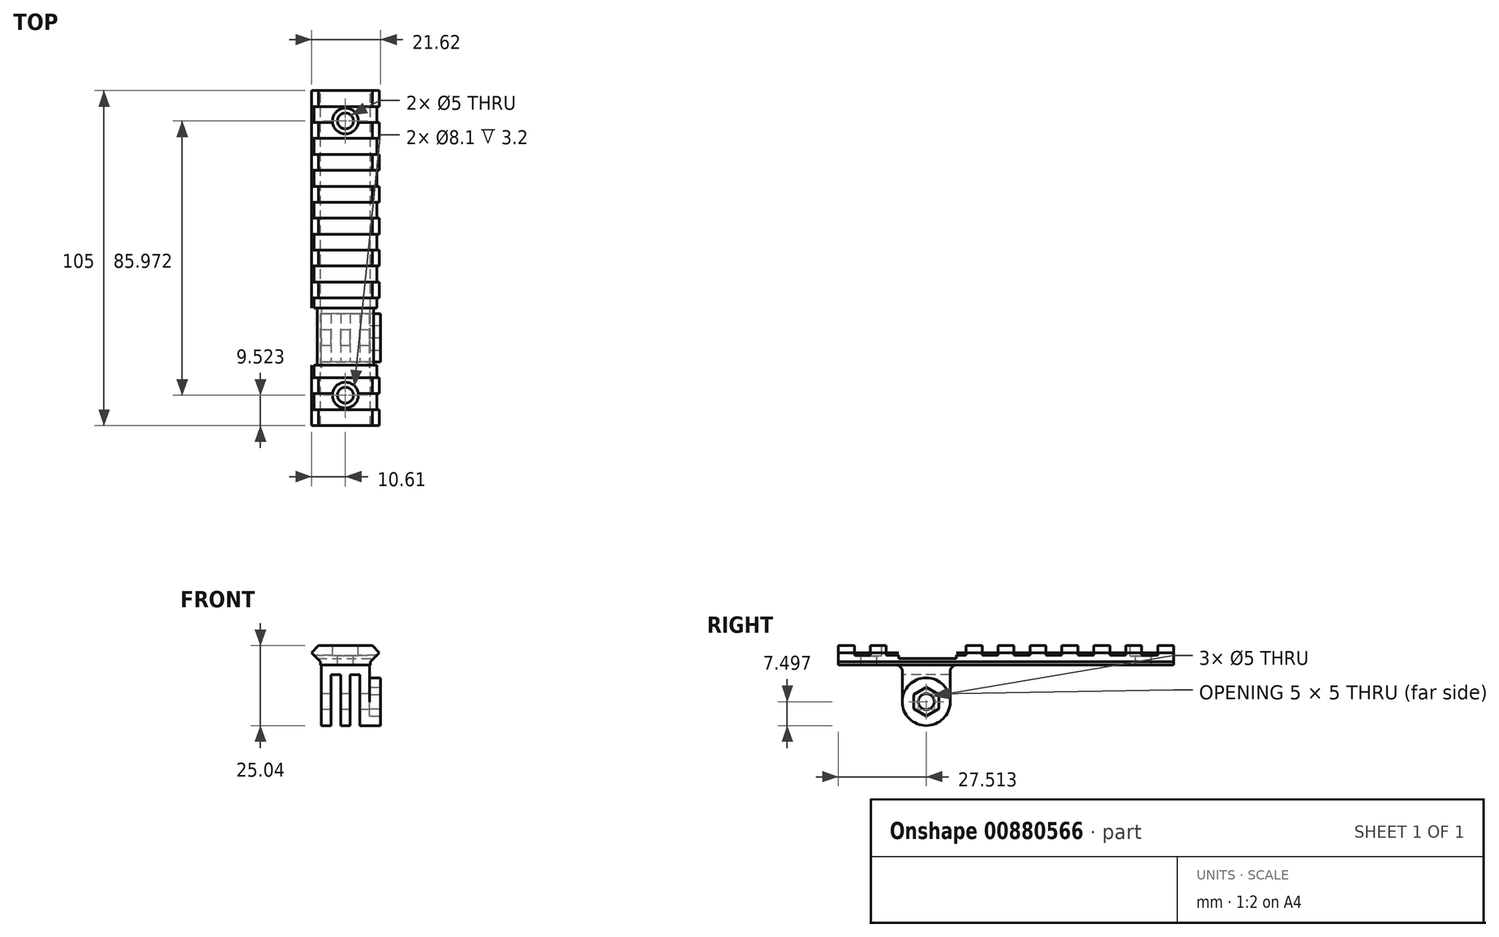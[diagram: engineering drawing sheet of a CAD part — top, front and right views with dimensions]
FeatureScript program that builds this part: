
annotation { "Feature Type Name" : "Feature", "Feature Type Description" : "" }
export const myFeature = defineFeature(function(context is Context, id is Id, definition is map)
    precondition{}
    {
        {
            var Q0;
            Q0=qCreatedBy(makeId("Front.planeOp"),FACE);
            var sketch = newSketch(context, id + "F0", { "sketchPlane" : qUnion([Q0])});
            skLineSegment(sketch, "E0", {"start": v(-7.8, -3.01) * mm, "end": v(7.81, -3.01) * mm});
            skLineSegment(sketch, "E1", {"start": v(7.81, -3.01) * mm, "end": v(7.81, -1.98) * mm});
            skLineSegment(sketch, "E2", {"start": v(7.81, -1.98) * mm, "end": v(10.6, 0.79) * mm});
            skLineSegment(sketch, "E3", {"start": v(10.6, 0.79) * mm, "end": v(8.39, 3.03) * mm});
            skLineSegment(sketch, "E4", {"start": v(8.39, 3.03) * mm, "end": v(-8.4, 3.03) * mm});
            skLineSegment(sketch, "E5", {"start": v(-8.4, 3.03) * mm, "end": v(-10.6, 0.79) * mm});
            skLineSegment(sketch, "E6", {"start": v(-10.6, 0.79) * mm, "end": v(-7.8, -1.98) * mm});
            skLineSegment(sketch, "E7", {"start": v(-7.8, -1.98) * mm, "end": v(-7.8, -3.01) * mm});
            skSolve(sketch);
        }
        {
            var Q0;
            Q0=qSketchRegion(id+"F0",true);
            extrude(context, id + "F1", {"entities" : qUnion([Q0]), "endBound" : BoundingType.SYMMETRIC, "depth" : 105 * mm, "offsetDistance" : 25 * mm});
        }
        {
            var Q0;
            Q0=qCreatedBy(makeId("Top.planeOp"),FACE);
            var sketch = newSketch(context, id + "F2", { "sketchPlane" : qUnion([Q0])});
            skLineSegment(sketch, "E8.bottom", {"start": v(10.61, -7.5) * mm, "end": v(-10.6, -7.5) * mm});
            skLineSegment(sketch, "E8.top", {"start": v(10.61, -2.5) * mm, "end": v(-10.6, -2.5) * mm});
            skLineSegment(sketch, "E8.left", {"start": v(10.61, -7.5) * mm, "end": v(10.61, -2.5) * mm});
            skLineSegment(sketch, "E8.right", {"start": v(-10.6, -7.5) * mm, "end": v(-10.6, -2.5) * mm});
            skLineSegment(sketch, "E9.0.1.0", {"start": v(10.61, -17.5) * mm, "end": v(-10.6, -17.5) * mm});
            skLineSegment(sketch, "E9.0.1.1", {"start": v(10.61, -12.5) * mm, "end": v(-10.6, -12.5) * mm});
            skLineSegment(sketch, "E9.0.1.2", {"start": v(10.61, -17.5) * mm, "end": v(10.61, -12.5) * mm});
            skLineSegment(sketch, "E9.0.1.3", {"start": v(-10.6, -17.5) * mm, "end": v(-10.6, -12.5) * mm});
            skLineSegment(sketch, "E9.0.2.0", {"start": v(10.61, -27.5) * mm, "end": v(-10.6, -27.5) * mm});
            skLineSegment(sketch, "E9.0.2.1", {"start": v(10.61, -22.5) * mm, "end": v(-10.6, -22.5) * mm});
            skLineSegment(sketch, "E9.0.2.2", {"start": v(10.61, -27.5) * mm, "end": v(10.61, -22.5) * mm});
            skLineSegment(sketch, "E9.0.2.3", {"start": v(-10.6, -27.5) * mm, "end": v(-10.6, -22.5) * mm});
            skLineSegment(sketch, "E9.0.3.0", {"start": v(10.61, -37.5) * mm, "end": v(-10.6, -37.5) * mm});
            skLineSegment(sketch, "E9.0.3.1", {"start": v(10.61, -32.5) * mm, "end": v(-10.6, -32.5) * mm});
            skLineSegment(sketch, "E9.0.3.2", {"start": v(10.61, -37.5) * mm, "end": v(10.61, -32.5) * mm});
            skLineSegment(sketch, "E9.0.3.3", {"start": v(-10.6, -37.5) * mm, "end": v(-10.6, -32.5) * mm});
            skLineSegment(sketch, "E9.0.4.0", {"start": v(10.61, -47.5) * mm, "end": v(-10.6, -47.5) * mm});
            skLineSegment(sketch, "E9.0.4.1", {"start": v(10.61, -42.5) * mm, "end": v(-10.6, -42.5) * mm});
            skLineSegment(sketch, "E9.0.4.2", {"start": v(10.61, -47.5) * mm, "end": v(10.61, -42.5) * mm});
            skLineSegment(sketch, "E9.0.4.3", {"start": v(-10.6, -47.5) * mm, "end": v(-10.6, -42.5) * mm});
            skLineSegment(sketch, "E9.direction1", {"start": v(-10.6, -7.5) * mm, "end": v(14.4, -7.5) * mm, "construction": true});
            skLineSegment(sketch, "E9.direction2", {"start": v(-10.6, -7.5) * mm, "end": v(-10.6, -17.5) * mm, "construction": true});
            skLineSegment(sketch, "E10.0.1.0", {"start": v(10.61, 7.5) * mm, "end": v(-10.6, 7.5) * mm});
            skLineSegment(sketch, "E10.0.1.1", {"start": v(10.61, 2.5) * mm, "end": v(10.61, 7.5) * mm});
            skLineSegment(sketch, "E10.0.1.2", {"start": v(-10.6, 2.5) * mm, "end": v(-10.6, 7.5) * mm});
            skLineSegment(sketch, "E10.0.1.3", {"start": v(10.61, 2.5) * mm, "end": v(-10.6, 2.5) * mm});
            skLineSegment(sketch, "E10.0.2.0", {"start": v(10.61, 17.5) * mm, "end": v(-10.6, 17.5) * mm});
            skLineSegment(sketch, "E10.0.2.1", {"start": v(10.61, 12.5) * mm, "end": v(10.61, 17.5) * mm});
            skLineSegment(sketch, "E10.0.2.2", {"start": v(-10.6, 12.5) * mm, "end": v(-10.6, 17.5) * mm});
            skLineSegment(sketch, "E10.0.2.3", {"start": v(10.61, 12.5) * mm, "end": v(-10.6, 12.5) * mm});
            skLineSegment(sketch, "E10.0.3.0", {"start": v(10.61, 27.5) * mm, "end": v(-10.6, 27.5) * mm});
            skLineSegment(sketch, "E10.0.3.1", {"start": v(10.61, 22.5) * mm, "end": v(10.61, 27.5) * mm});
            skLineSegment(sketch, "E10.0.3.2", {"start": v(-10.6, 22.5) * mm, "end": v(-10.6, 27.5) * mm});
            skLineSegment(sketch, "E10.0.3.3", {"start": v(10.61, 22.5) * mm, "end": v(-10.6, 22.5) * mm});
            skLineSegment(sketch, "E10.0.4.0", {"start": v(10.61, 37.5) * mm, "end": v(-10.6, 37.5) * mm});
            skLineSegment(sketch, "E10.0.4.1", {"start": v(10.61, 32.5) * mm, "end": v(10.61, 37.5) * mm});
            skLineSegment(sketch, "E10.0.4.2", {"start": v(-10.6, 32.5) * mm, "end": v(-10.6, 37.5) * mm});
            skLineSegment(sketch, "E10.0.4.3", {"start": v(10.61, 32.5) * mm, "end": v(-10.6, 32.5) * mm});
            skLineSegment(sketch, "E10.0.5.0", {"start": v(10.61, 47.5) * mm, "end": v(-10.6, 47.5) * mm});
            skLineSegment(sketch, "E10.0.5.1", {"start": v(10.61, 42.5) * mm, "end": v(10.61, 47.5) * mm});
            skLineSegment(sketch, "E10.0.5.2", {"start": v(-10.6, 42.5) * mm, "end": v(-10.6, 47.5) * mm});
            skLineSegment(sketch, "E10.0.5.3", {"start": v(10.61, 42.5) * mm, "end": v(-10.6, 42.5) * mm});
            skLineSegment(sketch, "E10.direction1", {"start": v(-10.6, -2.5) * mm, "end": v(14.4, -2.5) * mm, "construction": true});
            skLineSegment(sketch, "E10.direction2", {"start": v(-10.6, -2.5) * mm, "end": v(-10.6, 7.5) * mm, "construction": true});
            skSolve(sketch);
        }
        {
            var Q0;
            Q0=qSketchRegion(id+"F2",true);
            extrude(context, id + "F3", {"entities" : qUnion([Q0]), "operationType" : NewBodyOperationType.REMOVE, "depth" : 5 * mm, "offsetDistance" : 25 * mm});
        }
        {
            var Q0;
            Q0=makeQuery(id+"F3.boolean.opBoolean","SPLIT",FACE,{"disambiguationData":[TD([makeQuery(id+"F3.opExtrude","SWEPT_FACE",FACE,{"disambiguationData":[OSD([sQuery(id+"F2.wireOp",EDGE,"E10.0.4.0")])]})])],"derivedFrom":makeQuery(id+"F1.opExtrude","SWEPT_FACE",FACE,{"disambiguationData":[OSD([sQuery(id+"F0.wireOp",EDGE,"E4")])]})});
            var sketch = newSketch(context, id + "F4", { "sketchPlane" : qUnion([Q0])});
            skPoint(sketch, "E11", {"position": v(0, 43) * mm});
            skPoint(sketch, "E12", {"position": v(0, -42.98) * mm});
            skSolve(sketch);
        }
        {
            var Q0;
            Q0=sQuery(id+"F4.wireOp",VERTEX,"E11");
            var Q1;
            Q1=makeQuery(id+"F1.opExtrude","SWEPT_BODY",BODY,{"disambiguationData":[OSD([sQuery(id+"F0.wireOp",EDGE,"E0"),sQuery(id+"F0.wireOp",EDGE,"E1"),sQuery(id+"F0.wireOp",EDGE,"E2"),sQuery(id+"F0.wireOp",EDGE,"E3"),sQuery(id+"F0.wireOp",EDGE,"E4"),sQuery(id+"F0.wireOp",EDGE,"E5"),sQuery(id+"F0.wireOp",EDGE,"E6"),sQuery(id+"F0.wireOp",EDGE,"E7")])]});
            hole(context, id + "F5", {"style" : HoleStyle.C_BORE, "endStyle" : HoleEndStyle.BLIND, "holeDiameter" : 5 * mm, "cBoreDiameter" : 8.1 * mm, "cBoreDepth" : 3.2 * mm, "majorDiameter" : 5 * mm, "holeDepth" : 6.1 * mm, "isTappedThrough" : true, "tappedDepth" : 12 * mm, "tapClearance" : 3, "startFromSketch" : true, "locations" : qUnion([Q0]), "scope" : qUnion([Q1])});
        }
        {
            var Q0;
            Q0=sQuery(id+"F4.wireOp",VERTEX,"E12");
            var Q1;
            Q1=makeQuery(id+"F1.opExtrude","SWEPT_BODY",BODY,{"disambiguationData":[OSD([sQuery(id+"F0.wireOp",EDGE,"E0"),sQuery(id+"F0.wireOp",EDGE,"E1"),sQuery(id+"F0.wireOp",EDGE,"E2"),sQuery(id+"F0.wireOp",EDGE,"E3"),sQuery(id+"F0.wireOp",EDGE,"E4"),sQuery(id+"F0.wireOp",EDGE,"E5"),sQuery(id+"F0.wireOp",EDGE,"E6"),sQuery(id+"F0.wireOp",EDGE,"E7")])]});
            hole(context, id + "F6", {"style" : HoleStyle.C_BORE, "endStyle" : HoleEndStyle.BLIND, "holeDiameter" : 5 * mm, "cBoreDiameter" : 8.1 * mm, "cBoreDepth" : 3.2 * mm, "majorDiameter" : 5 * mm, "holeDepth" : 6.1 * mm, "isTappedThrough" : true, "tappedDepth" : 12 * mm, "tapClearance" : 3, "startFromSketch" : true, "locations" : qUnion([Q0]), "scope" : qUnion([Q1])});
        }
        {
            var Q0;
            Q0=makeQuery(id+"F1.opExtrude","SWEPT_FACE",FACE,{"disambiguationData":[OSD([sQuery(id+"F0.wireOp",EDGE,"E0")])]});
            var sketch = newSketch(context, id + "F7", { "sketchPlane" : qUnion([Q0])});
            skLineSegment(sketch, "E13.bottom", {"start": v(-114.09, 45.69) * mm, "end": v(-86.59, 45.69) * mm});
            skLineSegment(sketch, "E13.top", {"start": v(-114.09, 30.69) * mm, "end": v(-86.59, 30.69) * mm});
            skLineSegment(sketch, "E13.left", {"start": v(-121.59, 38.19) * mm, "end": v(-121.59, 38.19) * mm});
            skLineSegment(sketch, "E13.right", {"start": v(-86.59, 45.69) * mm, "end": v(-86.59, 30.69) * mm});
            skLineSegment(sketch, "E14", {"start": v(-121.59, 30.69) * mm, "end": v(-86.59, 45.69) * mm, "construction": true});
            skLineSegment(sketch, "E15", {"start": v(-121.59, 45.69) * mm, "end": v(-86.59, 30.69) * mm, "construction": true});
            skPoint(sketch, "E16.visualSharp", {"position": v(-121.59, 45.69) * mm});
            skArc(sketch, "E16.filletArc", {"start": v(-114.09, 45.69) * mm, "mid": v(-119.4, 43.5) * mm, "end": v(-121.59, 38.19) * mm});
            skPoint(sketch, "E17.visualSharp", {"position": v(-121.59, 30.69) * mm});
            skArc(sketch, "E17.filletArc", {"start": v(-121.59, 38.19) * mm, "mid": v(-119.4, 32.88) * mm, "end": v(-114.09, 30.69) * mm});
            skCircle(sketch, "E18", {"center": v(-114.09, 38.19) * mm, "radius": 2.5 * mm});
            skCircle(sketch, "E19", {"center": v(-114.09, 38.19) * mm, "radius": 7.5 * mm});
            skSolve(sketch);
        }
        {
            var Q0;
            Q0 = qSketchRegion(id + "F7", true);
            extrude(context, id + "F8", {"entities" : qUnion([Q0]), "depth" : 15 * mm, "offsetDistance" : 25 * mm});
        }
        {
            var Q0;
            Q0=makeQuery(id+"F7.imprint","IMPRINT",FACE,{"disambiguationData":[TD([[makeQuery(id+"F7.imprint","IMPRINT",EDGE,{"derivedFrom":sQuery(id+"F7.wireOp",EDGE,"E18")}),-1.0]])]});
            extrude(context, id + "F9", {"entities" : qUnion([Q0]), "operationType" : NewBodyOperationType.ADD, "depth" : 18.5 * mm, "offsetDistance" : 25 * mm});
        }
        {
            var Q0;
            Q0=makeQuery(id+"F9.opExtrude","CAP_FACE",FACE,{"disambiguationData":[OSD([sQuery(id+"F7.wireOp",EDGE,"E18"),sQuery(id+"F7.wireOp",EDGE,"E19")])],"isStart":false});
            var sketch = newSketch(context, id + "F10", { "sketchPlane" : qUnion([Q0])});
            skLineSegment(sketch, "E20", {"start": v(-114.09, 38.19) * mm, "end": v(-109.59, 38.19) * mm, "construction": true});
            skCircle(sketch, "E21.cCircle", {"center": v(-114.09, 38.19) * mm, "radius": 4.5 * mm, "construction": true});
            skLineSegment(sketch, "E21.0", {"start": v(-109.59, 38.19) * mm, "end": v(-111.84, 34.3) * mm});
            skLineSegment(sketch, "E21.1", {"start": v(-111.84, 34.3) * mm, "end": v(-116.34, 34.3) * mm});
            skLineSegment(sketch, "E21.2", {"start": v(-116.34, 34.3) * mm, "end": v(-118.59, 38.19) * mm});
            skLineSegment(sketch, "E21.3", {"start": v(-118.59, 38.19) * mm, "end": v(-116.34, 42.08) * mm});
            skLineSegment(sketch, "E21.4", {"start": v(-116.34, 42.08) * mm, "end": v(-111.84, 42.08) * mm});
            skLineSegment(sketch, "E21.5", {"start": v(-111.84, 42.08) * mm, "end": v(-109.59, 38.19) * mm});
            skSolve(sketch);
        }
        {
            var Q0;
            Q0 = qSketchRegion(id + "F10", true);
            extrude(context, id + "F11", {"entities" : qUnion([Q0]), "operationType" : NewBodyOperationType.REMOVE, "oppositeDirection" : true, "depth" : 3.5 * mm, "offsetDistance" : 25 * mm});
        }
        {
            var Q0;
            Q0=makeQuery(id+"F8.opExtrude","CAP_FACE",FACE,{"disambiguationData":[OSD([sQuery(id+"F7.wireOp",EDGE,"E13.bottom"),sQuery(id+"F7.wireOp",EDGE,"E13.top"),sQuery(id+"F7.wireOp",EDGE,"E13.right"),sQuery(id+"F7.wireOp",EDGE,"E18"),sQuery(id+"F7.wireOp",EDGE,"E19")])],"isStart":true});
            var sketch = newSketch(context, id + "F12", { "sketchPlane" : qUnion([Q0])});
            skLineSegment(sketch, "E22.bottom", {"start": v(-105.66, -30.69) * mm, "end": v(-121.66, -30.69) * mm});
            skLineSegment(sketch, "E22.top", {"start": v(-105.66, -45.69) * mm, "end": v(-121.66, -45.69) * mm});
            skLineSegment(sketch, "E22.left", {"start": v(-105.66, -30.69) * mm, "end": v(-105.66, -45.69) * mm});
            skLineSegment(sketch, "E22.right", {"start": v(-121.66, -30.69) * mm, "end": v(-121.66, -45.69) * mm});
            skSolve(sketch);
        }
        {
            var Q0;
            Q0 = qSketchRegion(id + "F12", true);
            extrude(context, id + "F13", {"entities" : qUnion([Q0]), "operationType" : NewBodyOperationType.REMOVE, "oppositeDirection" : true, "depth" : 6 * mm, "offsetDistance" : 25 * mm, "hasSecondDirection" : true, "secondDirectionOppositeDirection" : true, "secondDirectionDepth" : 3 * mm});
        }
        {
            var Q0;
            Q0 = qSketchRegion(id + "F12", true);
            extrude(context, id + "F14", {"entities" : qUnion([Q0]), "operationType" : NewBodyOperationType.REMOVE, "oppositeDirection" : true, "depth" : 12 * mm, "offsetDistance" : 25 * mm, "hasSecondDirection" : true, "secondDirectionOppositeDirection" : true, "secondDirectionDepth" : 9 * mm});
        }
        {
            var Q0;
            Q0=makeQuery(id+"F8.opExtrude","SWEPT_BODY",BODY,{"disambiguationData":[OSD([sQuery(id+"F7.wireOp",EDGE,"E13.bottom"),sQuery(id+"F7.wireOp",EDGE,"E13.top"),sQuery(id+"F7.wireOp",EDGE,"E13.right"),sQuery(id+"F7.wireOp",EDGE,"E18"),sQuery(id+"F7.wireOp",EDGE,"E19")])]});
            var Q1;
            Q1=makeQuery(id+"F8.opExtrude","CAP_EDGE",EDGE,{"disambiguationData":[OSD([sQuery(id+"F7.wireOp",EDGE,"E13.right")])],"isStart":false});
            transform(context, id + "F15", {"entities" : qUnion([Q0]), "transformType" : TransformType.ROTATION, "transformAxis" : qUnion([Q1]), "angle" : 90 * degree, "oppositeDirection" : true, "makeCopy" : false});
        }
        {
            var Q0;
            Q0=makeQuery(id+"F8.opExtrude","SWEPT_BODY",BODY,{"disambiguationData":[OSD([sQuery(id+"F7.wireOp",EDGE,"E13.bottom"),sQuery(id+"F7.wireOp",EDGE,"E13.top"),sQuery(id+"F7.wireOp",EDGE,"E13.right"),sQuery(id+"F7.wireOp",EDGE,"E18"),sQuery(id+"F7.wireOp",EDGE,"E19")])]});
            transform(context, id + "F16", {"entities" : qUnion([Q0]), "transformType" : TransformType.TRANSLATION_3D, "dx" : 94.1 * mm, "dy" : 0 * mm, "dz" : 31 * mm, "makeCopy" : false});
        }
        {
            var Q0;
            Q0=makeQuery(id+"F8.opExtrude","SWEPT_BODY",BODY,{"disambiguationData":[OSD([sQuery(id+"F7.wireOp",EDGE,"E13.bottom"),sQuery(id+"F7.wireOp",EDGE,"E13.top"),sQuery(id+"F7.wireOp",EDGE,"E13.right"),sQuery(id+"F7.wireOp",EDGE,"E18"),sQuery(id+"F7.wireOp",EDGE,"E19")])]});
            transform(context, id + "F17", {"entities" : qUnion([Q0]), "transformType" : TransformType.TRANSLATION_3D, "dx" : 0 * mm, "dy" : 13.2 * mm, "dz" : 0 * mm, "makeCopy" : false});
        }
        {
            var Q0;
            Q0=makeQuery(id+"F8.opExtrude","SWEPT_FACE",FACE,{"disambiguationData":[OSD([sQuery(id+"F7.wireOp",EDGE,"E13.right")])]});
            var sketch = newSketch(context, id + "F18", { "sketchPlane" : qUnion([Q0])});
            skLineSegment(sketch, "E23.bottom", {"start": v(-11.8, -15.61) * mm, "end": v(13.2, -15.61) * mm});
            skLineSegment(sketch, "E23.top", {"start": v(-11.8, -33.61) * mm, "end": v(13.2, -33.61) * mm});
            skLineSegment(sketch, "E23.left", {"start": v(-11.8, -15.61) * mm, "end": v(-11.8, -33.61) * mm});
            skLineSegment(sketch, "E23.right", {"start": v(13.2, -15.61) * mm, "end": v(13.2, -33.61) * mm});
            skSolve(sketch);
        }
        {
            var Q0;
            Q0 = qSketchRegion(id + "F18", true);
            extrude(context, id + "F19", {"entities" : qUnion([Q0]), "operationType" : NewBodyOperationType.REMOVE, "oppositeDirection" : true, "depth" : 14 * mm, "offsetDistance" : 25 * mm});
        }
        {
            var Q0;
            Q0=makeQuery(id+"F1.opExtrude","SWEPT_BODY",BODY,{"disambiguationData":[OSD([sQuery(id+"F0.wireOp",EDGE,"E0"),sQuery(id+"F0.wireOp",EDGE,"E1"),sQuery(id+"F0.wireOp",EDGE,"E2"),sQuery(id+"F0.wireOp",EDGE,"E3"),sQuery(id+"F0.wireOp",EDGE,"E4"),sQuery(id+"F0.wireOp",EDGE,"E5"),sQuery(id+"F0.wireOp",EDGE,"E6"),sQuery(id+"F0.wireOp",EDGE,"E7")])]});
            var Q1;
            Q1=makeQuery(id+"F8.opExtrude","SWEPT_BODY",BODY,{"disambiguationData":[OSD([sQuery(id+"F7.wireOp",EDGE,"E13.bottom"),sQuery(id+"F7.wireOp",EDGE,"E13.top"),sQuery(id+"F7.wireOp",EDGE,"E13.right"),sQuery(id+"F7.wireOp",EDGE,"E18"),sQuery(id+"F7.wireOp",EDGE,"E19")])]});
            booleanBodies(context, id + "F20", {"operationType" : BooleanOperationType.UNION, "tools" : qUnion([Q0, Q1])});
        }
        {
            var Q0;
            Q0=makeQuery(id+"F20.opBoolean","INTERSECT",EDGE,{"derivedFrom":[makeQuery(id+"F1.opExtrude","SWEPT_FACE",FACE,{"disambiguationData":[OSD([sQuery(id+"F0.wireOp",EDGE,"E0")])]}),makeQuery(id+"F8.opExtrude","SWEPT_FACE",FACE,{"disambiguationData":[OSD([sQuery(id+"F7.wireOp",EDGE,"E13.bottom")])]})]});
            var Q1;
            Q1=makeQuery(id+"F20.opBoolean","INTERSECT",EDGE,{"derivedFrom":[makeQuery(id+"F1.opExtrude","SWEPT_FACE",FACE,{"disambiguationData":[OSD([sQuery(id+"F0.wireOp",EDGE,"E0")])]}),makeQuery(id+"F8.opExtrude","SWEPT_FACE",FACE,{"disambiguationData":[OSD([sQuery(id+"F7.wireOp",EDGE,"E13.top")])]})]});
            fillet(context, id + "F21", {"entities" : qUnion([Q0, Q1]), "radius" : 2 * mm, "tangentPropagation" : true, "allowEdgeOverflow" : false});
        }
    });
